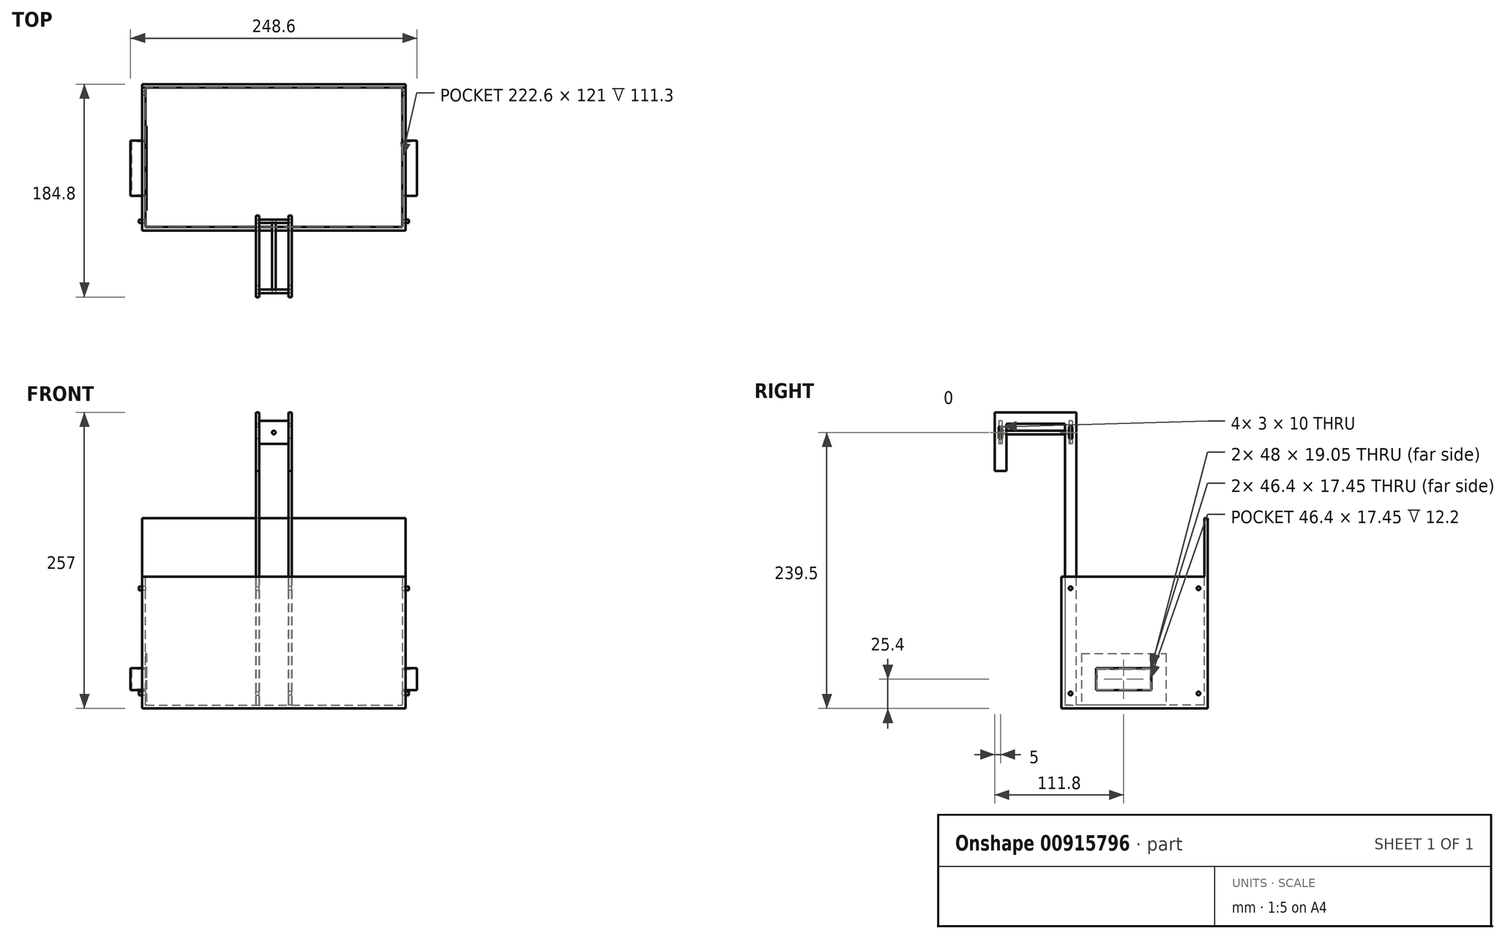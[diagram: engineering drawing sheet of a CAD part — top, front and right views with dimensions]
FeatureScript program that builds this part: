
annotation { "Feature Type Name" : "Feature", "Feature Type Description" : "" }
export const myFeature = defineFeature(function(context is Context, id is Id, definition is map)
    precondition{}
    {
        {
            var Q0;
            Q0=qCreatedBy(makeId("Front.planeOp"),FACE);
            var sketch = newSketch(context, id + "F0", { "sketchPlane" : qUnion([Q0])});
            skPoint(sketch, "E0.middle", {"position": v(0, 63.5) * mm});
            skPoint(sketch, "E1", {"position": v(56.2, 0) * mm});
            skLineSegment(sketch, "E2", {"start": v(-114.3, -3) * mm, "end": v(114.3, -3) * mm});
            skLineSegment(sketch, "E3", {"start": v(-114.3, -3) * mm, "end": v(-114.3, 111.3) * mm});
            skLineSegment(sketch, "E4", {"start": v(-114.3, 111.3) * mm, "end": v(114.3, 111.3) * mm});
            skLineSegment(sketch, "E5", {"start": v(114.3, 111.3) * mm, "end": v(114.3, -3) * mm});
            skPoint(sketch, "E6", {"position": v(0, -3) * mm});
            skSolve(sketch);
        }
        {
            var Q0;
            Q0=qCreatedBy(makeId("Right.planeOp"),FACE);
            cPlane(context, id + "F1", {"entities" : qUnion([Q0]), "cplaneType" : CPlaneType.OFFSET, "offset" : 12.7 * mm, "width" : 150 * mm, "height" : 150 * mm});
        }
        {
            var Q0;
            Q0=qCreatedBy(id+"F1.planeOp",FACE);
            var sketch = newSketch(context, id + "F2", { "sketchPlane" : qUnion([Q0])});
            skLineSegment(sketch, "E7", {"start": v(13, 0) * mm, "end": v(13, 254) * mm});
            skLineSegment(sketch, "E8", {"start": v(13, 254) * mm, "end": v(-57.8, 254) * mm});
            skLineSegment(sketch, "E9", {"start": v(-57.8, 254) * mm, "end": v(-57.8, 203.2) * mm});
            skLineSegment(sketch, "E10", {"start": v(-57.8, 203.2) * mm, "end": v(-47.8, 203.2) * mm});
            skLineSegment(sketch, "E11", {"start": v(-47.8, 203.2) * mm, "end": v(-47.8, 244) * mm});
            skLineSegment(sketch, "E12", {"start": v(-47.8, 244) * mm, "end": v(3, 244) * mm});
            skLineSegment(sketch, "E13", {"start": v(3, 244) * mm, "end": v(3, 0) * mm});
            skLineSegment(sketch, "E14", {"start": v(3, 0) * mm, "end": v(13, 0) * mm});
            skCircle(sketch, "E15", {"center": v(8, 10) * mm, "radius": 1.56 * mm});
            skPoint(sketch, "E16", {"position": v(8, 0) * mm});
            skCircle(sketch, "E17", {"center": v(8, 101.3) * mm, "radius": 1.56 * mm});
            skLineSegment(sketch, "E18.bottom", {"start": v(-54.3, 231.5) * mm, "end": v(-51.3, 231.5) * mm});
            skLineSegment(sketch, "E18.top", {"start": v(-54.3, 241.5) * mm, "end": v(-51.3, 241.5) * mm});
            skLineSegment(sketch, "E18.left", {"start": v(-54.3, 231.5) * mm, "end": v(-54.3, 241.5) * mm});
            skLineSegment(sketch, "E18.right", {"start": v(-51.3, 231.5) * mm, "end": v(-51.3, 241.5) * mm});
            skLineSegment(sketch, "E19", {"start": v(-57.8, 221.49) * mm, "end": v(-47.8, 221.49) * mm, "construction": true});
            skPoint(sketch, "E20", {"position": v(-52.8, 221.49) * mm});
            skPoint(sketch, "E21", {"position": v(-52.8, 231.5) * mm});
            skPoint(sketch, "E22", {"position": v(-57.8, 228.6) * mm});
            skPoint(sketch, "E23", {"position": v(-54.3, 236.5) * mm});
            skLineSegment(sketch, "E24.bottom", {"start": v(6.5, 231.5) * mm, "end": v(9.5, 231.5) * mm});
            skLineSegment(sketch, "E24.top", {"start": v(6.5, 241.5) * mm, "end": v(9.5, 241.5) * mm});
            skLineSegment(sketch, "E24.left", {"start": v(6.5, 231.5) * mm, "end": v(6.5, 241.5) * mm});
            skLineSegment(sketch, "E24.right", {"start": v(9.5, 231.5) * mm, "end": v(9.5, 241.5) * mm});
            skLineSegment(sketch, "E25", {"start": v(3, 222.12) * mm, "end": v(13, 222.12) * mm, "construction": true});
            skPoint(sketch, "E26", {"position": v(8, 222.12) * mm});
            skPoint(sketch, "E27", {"position": v(8, 231.5) * mm});
            skPoint(sketch, "E28", {"position": v(6.5, 236.5) * mm});
            skSolve(sketch);
        }
        {
            var Q0;
            Q0 = qSketchRegion(id + "F2", true);
            extrude(context, id + "F3", {"entities" : qUnion([Q0]), "depth" : 3 * mm, "offsetDistance" : 25 * mm});
        }
        {
            var Q0;
            Q0=makeQuery(id+"F3.opExtrude","SWEPT_BODY",BODY,{"disambiguationData":[OSD([sQuery(id+"F2.wireOp",EDGE,"E7"),sQuery(id+"F2.wireOp",EDGE,"E8"),sQuery(id+"F2.wireOp",EDGE,"E9"),sQuery(id+"F2.wireOp",EDGE,"E10"),sQuery(id+"F2.wireOp",EDGE,"E11"),sQuery(id+"F2.wireOp",EDGE,"E12"),sQuery(id+"F2.wireOp",EDGE,"E13"),sQuery(id+"F2.wireOp",EDGE,"E14")])]});
            var Q1;
            Q1=qCreatedBy(makeId("Right.planeOp"),FACE);
            mirror(context, id + "F4", {"entities" : qUnion([Q0]), "mirrorPlane" : qUnion([Q1])});
        }
        {
            var Q0;
            Q0=qCreatedBy(makeId("Right.planeOp"),FACE);
            cPlane(context, id + "F5", {"entities" : qUnion([Q0]), "cplaneType" : CPlaneType.OFFSET, "offset" : 120.65 * mm, "width" : 150 * mm, "height" : 150 * mm});
        }
        {
            var Q0;
            Q0=qCreatedBy(id+"F5.planeOp",FACE);
            var sketch = newSketch(context, id + "F6", { "sketchPlane" : qUnion([Q0])});
            skCircle(sketch, "E29", {"center": v(8, 10) * mm, "radius": 1.56 * mm});
            skSolve(sketch);
        }
        {
            var Q0;
            Q0 = qSketchRegion(id + "F6", true);
            extrude(context, id + "F7", {"entities" : qUnion([Q0]), "oppositeDirection" : true, "depth" : 241.3 * mm, "offsetDistance" : 25 * mm});
        }
        {
            var Q0;
            Q0=qCreatedBy(id+"F5.planeOp",FACE);
            var sketch = newSketch(context, id + "F8", { "sketchPlane" : qUnion([Q0])});
            skCircle(sketch, "E30", {"center": v(8, 101.3) * mm, "radius": 1.56 * mm});
            skSolve(sketch);
        }
        {
            var Q0;
            Q0 = qSketchRegion(id + "F8", true);
            extrude(context, id + "F9", {"entities" : qUnion([Q0]), "oppositeDirection" : true, "depth" : 241.3 * mm, "offsetDistance" : 25 * mm});
        }
        {
            var Q0;
            Q0=makeQuery(id+"F0.imprint","IMPRINT",FACE,{"disambiguationData":[TD([[makeQuery(id+"F0.imprint","IMPRINT",EDGE,{"derivedFrom":sQuery(id+"F0.wireOp",EDGE,"E2")}),1.0]])]});
            extrude(context, id + "F10", {"entities" : qUnion([Q0]), "oppositeDirection" : true, "depth" : 127 * mm, "offsetDistance" : 25 * mm});
        }
        {
            var Q0;
            Q0=makeQuery(id+"F10.opExtrude","SWEPT_FACE",FACE,{"disambiguationData":[OSD([sQuery(id+"F0.wireOp",EDGE,"E4")])]});
            shell(context, id + "F11", {"entities" : qUnion([Q0]), "thickness" : 3 * mm});
        }
        {
            var Q0;
            Q0=qCreatedBy(makeId("Front.planeOp"),FACE);
            cPlane(context, id + "F12", {"entities" : qUnion([Q0]), "cplaneType" : CPlaneType.OFFSET, "offset" : 6.5 * mm, "oppositeDirection" : true, "width" : 150 * mm, "height" : 150 * mm});
        }
        {
            var Q0;
            Q0=qCreatedBy(id+"F12.planeOp",FACE);
            var sketch = newSketch(context, id + "F13", { "sketchPlane" : qUnion([Q0])});
            skLineSegment(sketch, "E31.bottom", {"start": v(-12.7, 246.5) * mm, "end": v(12.7, 246.5) * mm});
            skLineSegment(sketch, "E31.top", {"start": v(-12.7, 226.5) * mm, "end": v(12.7, 226.5) * mm});
            skLineSegment(sketch, "E31.left", {"start": v(-12.7, 246.5) * mm, "end": v(-12.7, 241.5) * mm});
            skLineSegment(sketch, "E31.right", {"start": v(12.7, 246.5) * mm, "end": v(12.7, 241.5) * mm});
            skLineSegment(sketch, "E32.bottom", {"start": v(12.7, 241.5) * mm, "end": v(15.7, 241.5) * mm});
            skLineSegment(sketch, "E32.top", {"start": v(12.7, 231.5) * mm, "end": v(15.7, 231.5) * mm});
            skLineSegment(sketch, "E32.right", {"start": v(15.7, 241.5) * mm, "end": v(15.7, 231.5) * mm});
            skLineSegment(sketch, "E33.bottom", {"start": v(-12.7, 241.5) * mm, "end": v(-15.7, 241.5) * mm});
            skLineSegment(sketch, "E33.top", {"start": v(-12.7, 231.5) * mm, "end": v(-15.7, 231.5) * mm});
            skLineSegment(sketch, "E33.right", {"start": v(-15.7, 241.5) * mm, "end": v(-15.7, 231.5) * mm});
            skLineSegment(sketch, "E34.trimOffspring", {"start": v(-12.7, 231.5) * mm, "end": v(-12.7, 226.5) * mm});
            skLineSegment(sketch, "E35.trimOffspring", {"start": v(12.7, 231.5) * mm, "end": v(12.7, 226.5) * mm});
            skCircle(sketch, "E36", {"center": v(0, 236.5) * mm, "radius": 1.56 * mm});
            skPoint(sketch, "E37", {"position": v(0, 226.5) * mm});
            skPoint(sketch, "E38", {"position": v(15.7, 236.5) * mm});
            skSolve(sketch);
        }
        {
            var Q0;
            Q0 = qSketchRegion(id + "F13", true);
            extrude(context, id + "F14", {"entities" : qUnion([Q0]), "oppositeDirection" : true, "depth" : 3 * mm, "offsetDistance" : 25 * mm});
        }
        {
            var Q0;
            Q0=makeQuery(id+"F14.opExtrude","SWEPT_BODY",BODY,{"disambiguationData":[OSD([sQuery(id+"F13.wireOp",EDGE,"E31.bottom"),sQuery(id+"F13.wireOp",EDGE,"E31.top"),sQuery(id+"F13.wireOp",EDGE,"E31.left"),sQuery(id+"F13.wireOp",EDGE,"E31.right"),sQuery(id+"F13.wireOp",EDGE,"E32.bottom"),sQuery(id+"F13.wireOp",EDGE,"E32.top"),sQuery(id+"F13.wireOp",EDGE,"E32.right"),sQuery(id+"F13.wireOp",EDGE,"E33.bottom"),sQuery(id+"F13.wireOp",EDGE,"E33.top"),sQuery(id+"F13.wireOp",EDGE,"E33.right"),sQuery(id+"F13.wireOp",EDGE,"E34.trimOffspring"),sQuery(id+"F13.wireOp",EDGE,"E35.trimOffspring")])]});
            transform(context, id + "F15", {"entities" : qUnion([Q0]), "transformType" : TransformType.TRANSLATION_3D, "dx" : 0 * mm, "dy" : -60.8 * mm, "dz" : 0 * mm, "makeCopy" : true});
        }
        {
            var Q0;
            Q0=makeQuery(id+"F10.opExtrude","CAP_FACE",FACE,{"disambiguationData":[OSD([sQuery(id+"F0.wireOp",EDGE,"E2"),sQuery(id+"F0.wireOp",EDGE,"E3"),sQuery(id+"F0.wireOp",EDGE,"E4"),sQuery(id+"F0.wireOp",EDGE,"E5")])],"isStart":false});
            var sketch = newSketch(context, id + "F16", { "sketchPlane" : qUnion([Q0])});
            skLineSegment(sketch, "E39.bottom", {"start": v(-114.3, 111.3) * mm, "end": v(114.3, 111.3) * mm});
            skLineSegment(sketch, "E39.top", {"start": v(-114.3, 162.1) * mm, "end": v(114.3, 162.1) * mm});
            skLineSegment(sketch, "E39.left", {"start": v(-114.3, 111.3) * mm, "end": v(-114.3, 162.1) * mm});
            skLineSegment(sketch, "E39.right", {"start": v(114.3, 111.3) * mm, "end": v(114.3, 162.1) * mm});
            skSolve(sketch);
        }
        {
            var Q0;
            Q0 = qSketchRegion(id + "F16", true);
            extrude(context, id + "F17", {"entities" : qUnion([Q0]), "oppositeDirection" : true, "depth" : 3 * mm, "offsetDistance" : 25 * mm});
        }
        {
            var Q0;
            Q0=makeQuery(id+"F17.opExtrude","SWEPT_BODY",BODY,{"disambiguationData":[OSD([sQuery(id+"F16.wireOp",EDGE,"E39.bottom"),sQuery(id+"F16.wireOp",EDGE,"E39.top"),sQuery(id+"F16.wireOp",EDGE,"E39.left"),sQuery(id+"F16.wireOp",EDGE,"E39.right")])]});
            var Q1;
            Q1=makeQuery(id+"F10.opExtrude","SWEPT_BODY",BODY,{"disambiguationData":[OSD([sQuery(id+"F0.wireOp",EDGE,"E2"),sQuery(id+"F0.wireOp",EDGE,"E3"),sQuery(id+"F0.wireOp",EDGE,"E4"),sQuery(id+"F0.wireOp",EDGE,"E5")])]});
            booleanBodies(context, id + "F18", {"operationType" : BooleanOperationType.UNION, "tools" : qUnion([Q0, Q1])});
        }
        {
            var Q0;
            Q0=makeQuery(id+"F15.opPattern","COPY",FACE,{"derivedFrom":makeQuery(id+"F14.opExtrude","CAP_FACE",FACE,{"disambiguationData":[OSD([sQuery(id+"F13.wireOp",EDGE,"E31.bottom"),sQuery(id+"F13.wireOp",EDGE,"E31.top"),sQuery(id+"F13.wireOp",EDGE,"E31.left"),sQuery(id+"F13.wireOp",EDGE,"E31.right"),sQuery(id+"F13.wireOp",EDGE,"E32.bottom"),sQuery(id+"F13.wireOp",EDGE,"E32.top"),sQuery(id+"F13.wireOp",EDGE,"E32.right"),sQuery(id+"F13.wireOp",EDGE,"E33.bottom"),sQuery(id+"F13.wireOp",EDGE,"E33.top"),sQuery(id+"F13.wireOp",EDGE,"E33.right"),sQuery(id+"F13.wireOp",EDGE,"E34.trimOffspring"),sQuery(id+"F13.wireOp",EDGE,"E35.trimOffspring"),sQuery(id+"F13.wireOp",EDGE,"E36")])],"isStart":true}),"instanceName":"1"});
            var sketch = newSketch(context, id + "F19", { "sketchPlane" : qUnion([Q0])});
            skCircle(sketch, "E40", {"center": v(0, 236.5) * mm, "radius": 1.56 * mm});
            skSolve(sketch);
        }
        {
            var Q0;
            Q0 = qSketchRegion(id + "F19", true);
            extrude(context, id + "F20", {"entities" : qUnion([Q0]), "oppositeDirection" : true, "depth" : 63.8 * mm, "offsetDistance" : 25 * mm});
        }
        {
            var Q0;
            Q0=makeQuery(id+"F18.opBoolean","MERGE",FACE,{"derivedFrom":[makeQuery(id+"F10.opExtrude","SWEPT_FACE",FACE,{"disambiguationData":[OSD([sQuery(id+"F0.wireOp",EDGE,"E5")])]}),makeQuery(id+"F17.opExtrude","SWEPT_FACE",FACE,{"disambiguationData":[OSD([sQuery(id+"F16.wireOp",EDGE,"E39.left")])]})]});
            var sketch = newSketch(context, id + "F21", { "sketchPlane" : qUnion([Q0])});
            skLineSegment(sketch, "E41.bottom", {"start": v(30, 31.93) * mm, "end": v(78, 31.93) * mm});
            skLineSegment(sketch, "E41.top", {"start": v(30, 12.88) * mm, "end": v(78, 12.88) * mm});
            skLineSegment(sketch, "E41.left", {"start": v(30, 31.93) * mm, "end": v(30, 12.88) * mm});
            skLineSegment(sketch, "E41.right", {"start": v(78, 31.93) * mm, "end": v(78, 12.88) * mm});
            skLineSegment(sketch, "E42", {"start": v(54, 31.93) * mm, "end": v(54, 12.88) * mm});
            skPoint(sketch, "E43", {"position": v(54, 22.4) * mm});
            skSolve(sketch);
        }
        {
            var Q0;
            Q0 = qSketchRegion(id + "F21", true);
            extrude(context, id + "F22", {"entities" : qUnion([Q0]), "operationType" : NewBodyOperationType.REMOVE, "oppositeDirection" : true, "depth" : 3 * mm, "offsetDistance" : 25 * mm});
        }
        {
            var Q0;
            Q0=makeQuery(id+"F18.opBoolean","MERGE",FACE,{"derivedFrom":[makeQuery(id+"F10.opExtrude","SWEPT_FACE",FACE,{"disambiguationData":[OSD([sQuery(id+"F0.wireOp",EDGE,"E3")])]}),makeQuery(id+"F17.opExtrude","SWEPT_FACE",FACE,{"disambiguationData":[OSD([sQuery(id+"F16.wireOp",EDGE,"E39.right")])]})]});
            var sketch = newSketch(context, id + "F23", { "sketchPlane" : qUnion([Q0])});
            skLineSegment(sketch, "E44.bottom", {"start": v(-78, 31.93) * mm, "end": v(-30, 31.93) * mm});
            skLineSegment(sketch, "E44.top", {"start": v(-78, 12.88) * mm, "end": v(-30, 12.88) * mm});
            skLineSegment(sketch, "E44.left", {"start": v(-78, 31.93) * mm, "end": v(-78, 12.88) * mm});
            skLineSegment(sketch, "E44.right", {"start": v(-30, 31.93) * mm, "end": v(-30, 12.88) * mm});
            skLineSegment(sketch, "E45", {"start": v(-54, 31.93) * mm, "end": v(-54, 12.88) * mm});
            skPoint(sketch, "E46", {"position": v(-54, 22.4) * mm});
            skSolve(sketch);
        }
        {
            var Q0;
            Q0 = qSketchRegion(id + "F23", true);
            extrude(context, id + "F24", {"entities" : qUnion([Q0]), "operationType" : NewBodyOperationType.REMOVE, "oppositeDirection" : true, "depth" : 3 * mm, "offsetDistance" : 25 * mm});
        }
        {
            var Q0;
            Q0=qCreatedBy(makeId("Right.planeOp"),FACE);
            cPlane(context, id + "F25", {"entities" : qUnion([Q0]), "cplaneType" : CPlaneType.OFFSET, "offset" : 114.3 * mm + 10 * mm, "oppositeDirection" : true, "width" : 150 * mm, "height" : 150 * mm});
        }
        {
            var Q0;
            Q0=qCreatedBy(id+"F25.planeOp",FACE);
            var sketch = newSketch(context, id + "F26", { "sketchPlane" : qUnion([Q0])});
            skLineSegment(sketch, "E47.bottom", {"start": v(78, 31.93) * mm, "end": v(30, 31.93) * mm});
            skLineSegment(sketch, "E47.top", {"start": v(78, 12.88) * mm, "end": v(30, 12.88) * mm});
            skLineSegment(sketch, "E47.left", {"start": v(78, 31.93) * mm, "end": v(78, 12.88) * mm});
            skLineSegment(sketch, "E47.right", {"start": v(30, 31.93) * mm, "end": v(30, 12.88) * mm});
            skSolve(sketch);
        }
        {
            var Q0;
            Q0 = qSketchRegion(id + "F26", true);
            extrude(context, id + "F27", {"entities" : qUnion([Q0]), "depth" : 13 * mm, "offsetDistance" : 25 * mm});
        }
        {
            var Q0;
            Q0=makeQuery(id+"F11.opShell","OFFSET_FACE",FACE,{"disambiguationData":[OSD([sQuery(id+"F0.wireOp",EDGE,"E3")])]});
            var sketch = newSketch(context, id + "F28", { "sketchPlane" : qUnion([Q0])});
            skLineSegment(sketch, "E48.bottom", {"start": v(17.3, 44.63) * mm, "end": v(90.7, 44.63) * mm});
            skLineSegment(sketch, "E48.top", {"start": v(17.3, 0.18) * mm, "end": v(90.7, 0.18) * mm});
            skLineSegment(sketch, "E48.left", {"start": v(17.3, 44.63) * mm, "end": v(17.3, 0.18) * mm});
            skLineSegment(sketch, "E48.right", {"start": v(90.7, 44.63) * mm, "end": v(90.7, 0.18) * mm});
            skLineSegment(sketch, "E49.bottom", {"start": v(30.8, 31.13) * mm, "end": v(77.2, 31.13) * mm});
            skLineSegment(sketch, "E49.top", {"start": v(30.8, 13.68) * mm, "end": v(77.2, 13.68) * mm});
            skLineSegment(sketch, "E49.left", {"start": v(30.8, 31.13) * mm, "end": v(30.8, 13.68) * mm});
            skLineSegment(sketch, "E49.right", {"start": v(77.2, 31.13) * mm, "end": v(77.2, 13.68) * mm});
            skPoint(sketch, "E50", {"position": v(54, 31.13) * mm});
            skPoint(sketch, "E51", {"position": v(77.2, 22.4) * mm});
            skSolve(sketch);
        }
        {
            var Q0;
            Q0=makeQuery(id+"F27.opExtrude","CAP_FACE",FACE,{"disambiguationData":[OSD([sQuery(id+"F26.wireOp",EDGE,"E47.bottom"),sQuery(id+"F26.wireOp",EDGE,"E47.top"),sQuery(id+"F26.wireOp",EDGE,"E47.left"),sQuery(id+"F26.wireOp",EDGE,"E47.right")])],"isStart":false});
            shell(context, id + "F29", {"entities" : qUnion([Q0]), "thickness" : 0.8 * mm});
        }
        {
            var Q0;
            Q0 = qSketchRegion(id + "F28", true);
            extrude(context, id + "F30", {"entities" : qUnion([Q0]), "depth" : 0.8 * mm, "offsetDistance" : 25 * mm});
        }
        {
            var Q0;
            Q0=makeQuery(id+"F27.opExtrude","SWEPT_BODY",BODY,{"disambiguationData":[OSD([sQuery(id+"F26.wireOp",EDGE,"E47.bottom"),sQuery(id+"F26.wireOp",EDGE,"E47.top"),sQuery(id+"F26.wireOp",EDGE,"E47.left"),sQuery(id+"F26.wireOp",EDGE,"E47.right")])]});
            var Q1;
            Q1=qCreatedBy(makeId("Right.planeOp"),FACE);
            mirror(context, id + "F31", {"entities" : qUnion([Q0]), "mirrorPlane" : qUnion([Q1])});
        }
        {
            var Q0;
            Q0=makeQuery(id+"F18.opBoolean","MERGE",FACE,{"derivedFrom":[makeQuery(id+"F10.opExtrude","SWEPT_FACE",FACE,{"disambiguationData":[OSD([sQuery(id+"F0.wireOp",EDGE,"E5")])]}),makeQuery(id+"F17.opExtrude","SWEPT_FACE",FACE,{"disambiguationData":[OSD([sQuery(id+"F16.wireOp",EDGE,"E39.left")])]})]});
            var sketch = newSketch(context, id + "F32", { "sketchPlane" : qUnion([Q0])});
            skCircle(sketch, "E52", {"center": v(8, 101.3) * mm, "radius": 1.56 * mm});
            skSolve(sketch);
        }
        {
            var Q0;
            Q0 = qSketchRegion(id + "F32", true);
            extrude(context, id + "F33", {"entities" : qUnion([Q0]), "operationType" : NewBodyOperationType.REMOVE, "oppositeDirection" : true, "depth" : 3 * mm, "offsetDistance" : 25 * mm});
        }
        {
            var Q0;
            Q0=makeQuery(id+"F18.opBoolean","MERGE",FACE,{"derivedFrom":[makeQuery(id+"F10.opExtrude","SWEPT_FACE",FACE,{"disambiguationData":[OSD([sQuery(id+"F0.wireOp",EDGE,"E5")])]}),makeQuery(id+"F17.opExtrude","SWEPT_FACE",FACE,{"disambiguationData":[OSD([sQuery(id+"F16.wireOp",EDGE,"E39.left")])]})]});
            var sketch = newSketch(context, id + "F34", { "sketchPlane" : qUnion([Q0])});
            skCircle(sketch, "E53", {"center": v(8, 10) * mm, "radius": 1.56 * mm});
            skSolve(sketch);
        }
        {
            var Q0;
            Q0 = qSketchRegion(id + "F34", true);
            extrude(context, id + "F35", {"entities" : qUnion([Q0]), "operationType" : NewBodyOperationType.REMOVE, "oppositeDirection" : true, "depth" : 3 * mm, "offsetDistance" : 25 * mm});
        }
        {
            var Q0;
            Q0=makeQuery(id+"F18.opBoolean","MERGE",FACE,{"derivedFrom":[makeQuery(id+"F10.opExtrude","SWEPT_FACE",FACE,{"disambiguationData":[OSD([sQuery(id+"F0.wireOp",EDGE,"E3")])]}),makeQuery(id+"F17.opExtrude","SWEPT_FACE",FACE,{"disambiguationData":[OSD([sQuery(id+"F16.wireOp",EDGE,"E39.right")])]})]});
            var sketch = newSketch(context, id + "F36", { "sketchPlane" : qUnion([Q0])});
            skCircle(sketch, "E54", {"center": v(-8, 101.3) * mm, "radius": 1.56 * mm});
            skSolve(sketch);
        }
        {
            var Q0;
            Q0 = qSketchRegion(id + "F36", true);
            extrude(context, id + "F37", {"entities" : qUnion([Q0]), "operationType" : NewBodyOperationType.REMOVE, "oppositeDirection" : true, "depth" : 3 * mm, "offsetDistance" : 25 * mm});
        }
        {
            var Q0;
            Q0=makeQuery(id+"F18.opBoolean","MERGE",FACE,{"derivedFrom":[makeQuery(id+"F10.opExtrude","SWEPT_FACE",FACE,{"disambiguationData":[OSD([sQuery(id+"F0.wireOp",EDGE,"E3")])]}),makeQuery(id+"F17.opExtrude","SWEPT_FACE",FACE,{"disambiguationData":[OSD([sQuery(id+"F16.wireOp",EDGE,"E39.right")])]})]});
            var sketch = newSketch(context, id + "F38", { "sketchPlane" : qUnion([Q0])});
            skCircle(sketch, "E55", {"center": v(-8, 10) * mm, "radius": 1.56 * mm});
            skSolve(sketch);
        }
        {
            var Q0;
            Q0=makeQuery(id+"F18.opBoolean","MERGE",FACE,{"derivedFrom":[makeQuery(id+"F10.opExtrude","SWEPT_FACE",FACE,{"disambiguationData":[OSD([sQuery(id+"F0.wireOp",EDGE,"E3")])]}),makeQuery(id+"F17.opExtrude","SWEPT_FACE",FACE,{"disambiguationData":[OSD([sQuery(id+"F16.wireOp",EDGE,"E39.right")])]})]});
            var sketch = newSketch(context, id + "F39", { "sketchPlane" : qUnion([Q0])});
            skSolve(sketch);
        }
        {
            var Q0;
            Q0 = qSketchRegion(id + "F38", true);
            extrude(context, id + "F40", {"entities" : qUnion([Q0]), "operationType" : NewBodyOperationType.REMOVE, "oppositeDirection" : true, "depth" : 3 * mm, "offsetDistance" : 25 * mm});
        }
        {
            var Q0;
            Q0=makeQuery(id+"F33.boolean.opBoolean","SPLIT",BODY,{"disambiguationData":[OD(0.0)],"derivedFrom":makeQuery(id+"F9.opExtrude","SWEPT_BODY",BODY,{"disambiguationData":[OSD([sQuery(id+"F8.wireOp",EDGE,"E30")])]})});
            var Q1;
            Q1=makeQuery(id+"F37.boolean.opBoolean","SPLIT",BODY,{"disambiguationData":[OD(0.0)],"derivedFrom":makeQuery(id+"F33.boolean.opBoolean","SPLIT",BODY,{"disambiguationData":[OD(1.0)],"derivedFrom":makeQuery(id+"F9.opExtrude","SWEPT_BODY",BODY,{"disambiguationData":[OSD([sQuery(id+"F8.wireOp",EDGE,"E30")])]})})});
            deleteBodies(context, id + "F41", {"entities" : qUnion([Q0, Q1])});
        }
        {
            var Q0;
            Q0=makeQuery(id+"F11.opShell","OFFSET_FACE",FACE,{"disambiguationData":[OSD([sQuery(id+"F0.wireOp",EDGE,"E3")])]});
            var sketch = newSketch(context, id + "F42", { "sketchPlane" : qUnion([Q0])});
            skCircle(sketch, "E56", {"center": v(8, 101.3) * mm, "radius": 1.56 * mm});
            skSolve(sketch);
        }
        {
            var Q0;
            Q0 = qSketchRegion(id + "F42", true);
            extrude(context, id + "F43", {"entities" : qUnion([Q0]), "oppositeDirection" : true, "depth" : 6 * mm, "offsetDistance" : 25 * mm});
        }
        {
            var Q0;
            Q0=makeQuery(id+"F11.opShell","OFFSET_FACE",FACE,{"disambiguationData":[OSD([sQuery(id+"F0.wireOp",EDGE,"E5")])]});
            var sketch = newSketch(context, id + "F44", { "sketchPlane" : qUnion([Q0])});
            skCircle(sketch, "E57", {"center": v(-8, 101.3) * mm, "radius": 1.56 * mm});
            skSolve(sketch);
        }
        {
            var Q0;
            Q0 = qSketchRegion(id + "F44", true);
            extrude(context, id + "F45", {"entities" : qUnion([Q0]), "oppositeDirection" : true, "depth" : 6 * mm, "offsetDistance" : 25 * mm});
        }
        {
            var Q0;
            Q0=makeQuery(id+"F40.boolean.opBoolean","SPLIT",BODY,{"disambiguationData":[OD(0.0)],"derivedFrom":makeQuery(id+"F35.boolean.opBoolean","SPLIT",BODY,{"disambiguationData":[OD(1.0)],"derivedFrom":makeQuery(id+"F7.opExtrude","SWEPT_BODY",BODY,{"disambiguationData":[OSD([sQuery(id+"F6.wireOp",EDGE,"E29")])]})})});
            var Q1;
            Q1=makeQuery(id+"F35.boolean.opBoolean","SPLIT",BODY,{"disambiguationData":[OD(0.0)],"derivedFrom":makeQuery(id+"F7.opExtrude","SWEPT_BODY",BODY,{"disambiguationData":[OSD([sQuery(id+"F6.wireOp",EDGE,"E29")])]})});
            deleteBodies(context, id + "F46", {"entities" : qUnion([Q0, Q1])});
        }
        {
            var Q0;
            Q0=makeQuery(id+"F11.opShell","OFFSET_FACE",FACE,{"disambiguationData":[OSD([sQuery(id+"F0.wireOp",EDGE,"E3")])]});
            var sketch = newSketch(context, id + "F47", { "sketchPlane" : qUnion([Q0])});
            skCircle(sketch, "E58", {"center": v(8, 10) * mm, "radius": 1.56 * mm});
            skSolve(sketch);
        }
        {
            var Q0;
            Q0 = qSketchRegion(id + "F47", true);
            extrude(context, id + "F48", {"entities" : qUnion([Q0]), "oppositeDirection" : true, "depth" : 6 * mm, "offsetDistance" : 25 * mm});
        }
        {
            var Q0;
            Q0=makeQuery(id+"F11.opShell","OFFSET_FACE",FACE,{"disambiguationData":[OSD([sQuery(id+"F0.wireOp",EDGE,"E5")])]});
            var sketch = newSketch(context, id + "F49", { "sketchPlane" : qUnion([Q0])});
            skCircle(sketch, "E59", {"center": v(-8, 10) * mm, "radius": 1.56 * mm});
            skSolve(sketch);
        }
        {
            var Q0;
            Q0 = qSketchRegion(id + "F49", true);
            extrude(context, id + "F50", {"entities" : qUnion([Q0]), "oppositeDirection" : true, "depth" : 6 * mm, "offsetDistance" : 25 * mm});
        }
        {
            var Q0;
            Q0=makeQuery(id+"F18.opBoolean","MERGE",FACE,{"derivedFrom":[makeQuery(id+"F10.opExtrude","SWEPT_FACE",FACE,{"disambiguationData":[OSD([sQuery(id+"F0.wireOp",EDGE,"E5")])]}),makeQuery(id+"F17.opExtrude","SWEPT_FACE",FACE,{"disambiguationData":[OSD([sQuery(id+"F16.wireOp",EDGE,"E39.left")])]})]});
            var sketch = newSketch(context, id + "F51", { "sketchPlane" : qUnion([Q0])});
            skCircle(sketch, "E60", {"center": v(119, 101.3) * mm, "radius": 1.56 * mm});
            skSolve(sketch);
        }
        {
            var Q0;
            Q0 = qSketchRegion(id + "F51", true);
            extrude(context, id + "F52", {"entities" : qUnion([Q0]), "operationType" : NewBodyOperationType.REMOVE, "oppositeDirection" : true, "depth" : 3 * mm, "offsetDistance" : 25 * mm});
        }
        {
            var Q0;
            Q0=makeQuery(id+"F18.opBoolean","MERGE",FACE,{"derivedFrom":[makeQuery(id+"F10.opExtrude","SWEPT_FACE",FACE,{"disambiguationData":[OSD([sQuery(id+"F0.wireOp",EDGE,"E5")])]}),makeQuery(id+"F17.opExtrude","SWEPT_FACE",FACE,{"disambiguationData":[OSD([sQuery(id+"F16.wireOp",EDGE,"E39.left")])]})]});
            var sketch = newSketch(context, id + "F53", { "sketchPlane" : qUnion([Q0])});
            skCircle(sketch, "E61", {"center": v(119, 10) * mm, "radius": 1.56 * mm});
            skSolve(sketch);
        }
        {
            var Q0;
            Q0 = qSketchRegion(id + "F53", true);
            extrude(context, id + "F54", {"entities" : qUnion([Q0]), "operationType" : NewBodyOperationType.REMOVE, "oppositeDirection" : true, "depth" : 3 * mm, "offsetDistance" : 25 * mm});
        }
        {
            var Q0;
            {var subQ0=sQuery(id+"F0.wireOp",EDGE,"E3");Q0=makeQuery(id+"F39.imprint","IMPRINT",FACE,{"disambiguationData":[TD([[makeQuery(id+"F39.imprint","IMPRINT",EDGE,{"derivedFrom":makeQuery(id+"F10.opExtrude","CAP_EDGE",EDGE,{"disambiguationData":[OSD([subQ0])],"isStart":true})}),1.0]])]});}
            var sketch = newSketch(context, id + "F55", { "sketchPlane" : qUnion([Q0])});
            skCircle(sketch, "E62", {"center": v(-119, 101.3) * mm, "radius": 1.56 * mm});
            skSolve(sketch);
        }
        {
            var Q0;
            Q0 = qSketchRegion(id + "F55", true);
            extrude(context, id + "F56", {"entities" : qUnion([Q0]), "operationType" : NewBodyOperationType.REMOVE, "oppositeDirection" : true, "depth" : 3 * mm, "offsetDistance" : 25 * mm});
        }
        {
            var Q0;
            {var subQ0=sQuery(id+"F0.wireOp",EDGE,"E3");Q0=makeQuery(id+"F39.imprint","IMPRINT",FACE,{"disambiguationData":[TD([[makeQuery(id+"F39.imprint","IMPRINT",EDGE,{"derivedFrom":makeQuery(id+"F10.opExtrude","CAP_EDGE",EDGE,{"disambiguationData":[OSD([subQ0])],"isStart":true})}),1.0]])]});}
            var sketch = newSketch(context, id + "F57", { "sketchPlane" : qUnion([Q0])});
            skCircle(sketch, "E63", {"center": v(-119, 10) * mm, "radius": 1.56 * mm});
            skSolve(sketch);
        }
        {
            var Q0;
            Q0 = qSketchRegion(id + "F57", true);
            extrude(context, id + "F58", {"entities" : qUnion([Q0]), "operationType" : NewBodyOperationType.REMOVE, "oppositeDirection" : true, "depth" : 3 * mm, "offsetDistance" : 25 * mm});
        }
    });
